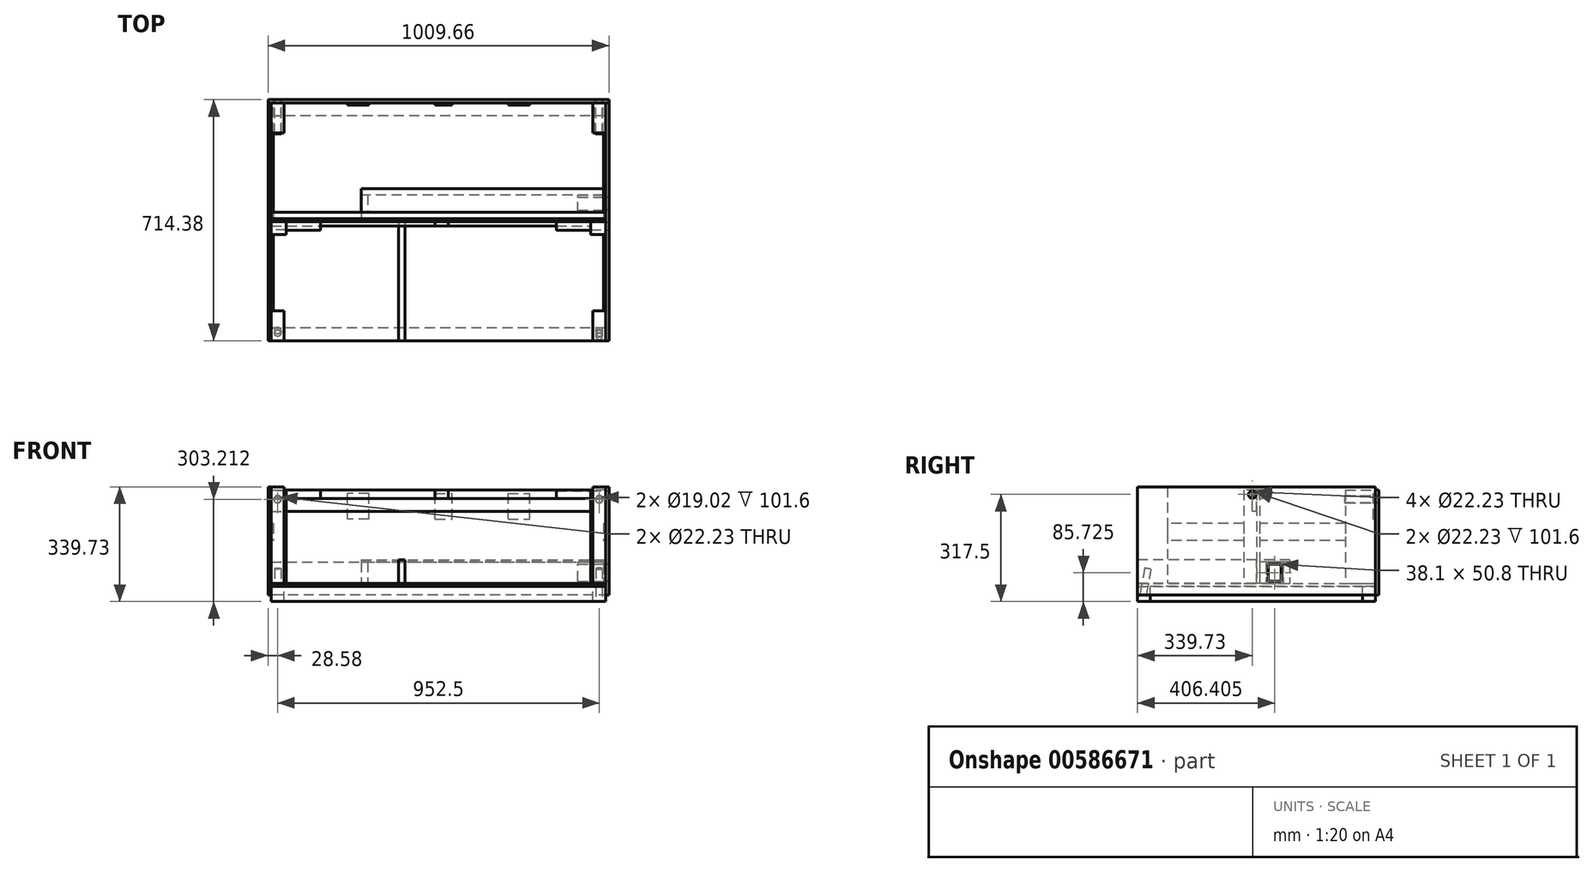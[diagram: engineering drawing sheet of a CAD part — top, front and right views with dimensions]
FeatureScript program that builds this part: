
annotation { "Feature Type Name" : "Feature", "Feature Type Description" : "" }
export const myFeature = defineFeature(function(context is Context, id is Id, definition is map)
    precondition{}
    {
        {
            var Q0;
            Q0=qCreatedBy(makeId("Right.planeOp"),FACE);
            var sketch = newSketch(context, id + "F0", { "sketchPlane" : qUnion([Q0])});
            skLineSegment(sketch, "E0.bottom", {"start": v(-352.43, 0) * mm, "end": v(-314.33, 0) * mm});
            skLineSegment(sketch, "E0.top", {"start": v(-352.43, 44.45) * mm, "end": v(-314.33, 44.45) * mm});
            skLineSegment(sketch, "E0.left", {"start": v(-352.43, 0) * mm, "end": v(-352.43, 44.45) * mm});
            skLineSegment(sketch, "E0.right", {"start": v(-314.33, 0) * mm, "end": v(-314.33, 44.45) * mm});
            skSolve(sketch);
        }
        {
            var Q0;
            Q0 = qSketchRegion(id + "F0", true);
            extrude(context, id + "F1", {"entities" : qUnion([Q0]), "endBound" : BoundingType.SYMMETRIC, "depth" : 990.6 * mm, "offsetDistance" : 25.4 * mm});
        }
        {
            var Q0;
            Q0=makeQuery(id+"F1.opExtrude","SWEPT_BODY",BODY,{"disambiguationData":[OSD([sQuery(id+"F0.wireOp",EDGE,"E0.bottom"),sQuery(id+"F0.wireOp",EDGE,"E0.top"),sQuery(id+"F0.wireOp",EDGE,"E0.left"),sQuery(id+"F0.wireOp",EDGE,"E0.right")])]});
            var Q1;
            Q1=qCreatedBy(makeId("Front.planeOp"),FACE);
            mirror(context, id + "F2", {"entities" : qUnion([Q0]), "mirrorPlane" : qUnion([Q1])});
        }
        {
            var Q0;
            Q0=makeQuery(id+"F1.opExtrude","SWEPT_FACE",FACE,{"disambiguationData":[OSD([sQuery(id+"F0.wireOp",EDGE,"E0.right")])]});
            var sketch = newSketch(context, id + "F3", { "sketchPlane" : qUnion([Q0])});
            skLineSegment(sketch, "E1.bottom", {"start": v(-495.3, 0) * mm, "end": v(-457.2, 0) * mm});
            skLineSegment(sketch, "E1.top", {"start": v(-495.3, 44.45) * mm, "end": v(-457.2, 44.45) * mm});
            skLineSegment(sketch, "E1.left", {"start": v(-495.3, 0) * mm, "end": v(-495.3, 44.45) * mm});
            skLineSegment(sketch, "E1.right", {"start": v(-457.2, 0) * mm, "end": v(-457.2, 44.45) * mm});
            skSolve(sketch);
        }
        {
            var Q0;
            Q0 = qSketchRegion(id + "F3", true);
            var Q1;
            Q1=makeQuery(id+"F2.opPattern","COPY",FACE,{"derivedFrom":makeQuery(id+"F1.opExtrude","SWEPT_FACE",FACE,{"disambiguationData":[OSD([sQuery(id+"F0.wireOp",EDGE,"E0.right")])]}),"instanceName":"1"});
            extrude(context, id + "F4", {"entities" : qUnion([Q0]), "endBound" : BoundingType.UP_TO_SURFACE, "depth" : 25.4 * mm, "endBoundEntityFace" : qUnion([Q1]), "offsetDistance" : 25.4 * mm});
        }
        {
            var Q0;
            Q0=makeQuery(id+"F4.opExtrude","SWEPT_BODY",BODY,{"disambiguationData":[OSD([sQuery(id+"F3.wireOp",EDGE,"E1.bottom"),sQuery(id+"F3.wireOp",EDGE,"E1.top"),sQuery(id+"F3.wireOp",EDGE,"E1.left"),sQuery(id+"F3.wireOp",EDGE,"E1.right")])]});
            var Q1;
            Q1=qCreatedBy(makeId("Right.planeOp"),FACE);
            mirror(context, id + "F5", {"entities" : qUnion([Q0]), "mirrorPlane" : qUnion([Q1])});
        }
        {
            var Q0;
            Q0=makeQuery(id+"F1.opExtrude","SWEPT_FACE",FACE,{"disambiguationData":[OSD([sQuery(id+"F0.wireOp",EDGE,"E0.top")])]});
            var sketch = newSketch(context, id + "F6", { "sketchPlane" : qUnion([Q0])});
            skLineSegment(sketch, "E2.bottom", {"start": v(-495.3, -352.43) * mm, "end": v(495.3, -352.43) * mm});
            skLineSegment(sketch, "E2.top", {"start": v(-495.3, 352.43) * mm, "end": v(495.3, 352.43) * mm});
            skLineSegment(sketch, "E2.left", {"start": v(-495.3, -352.43) * mm, "end": v(-495.3, 352.43) * mm});
            skLineSegment(sketch, "E2.right", {"start": v(495.3, -352.43) * mm, "end": v(495.3, 352.43) * mm});
            skSolve(sketch);
        }
        {
            var Q0;
            Q0 = qSketchRegion(id + "F6", true);
            extrude(context, id + "F7", {"entities" : qUnion([Q0]), "depth" : 9.52 * mm, "offsetDistance" : 25.4 * mm});
        }
        {
            var Q0;
            Q0=makeQuery(id+"F2.opPattern","COPY",FACE,{"derivedFrom":makeQuery(id+"F1.opExtrude","SWEPT_FACE",FACE,{"disambiguationData":[OSD([sQuery(id+"F0.wireOp",EDGE,"E0.left")])]}),"instanceName":"1"});
            var sketch = newSketch(context, id + "F8", { "sketchPlane" : qUnion([Q0])});
            skLineSegment(sketch, "E3.bottom", {"start": v(-504.83, 19.05) * mm, "end": v(504.83, 19.05) * mm});
            skLineSegment(sketch, "E3.top", {"start": v(-504.83, 330.2) * mm, "end": v(504.83, 330.2) * mm});
            skLineSegment(sketch, "E3.left", {"start": v(-504.83, 19.05) * mm, "end": v(-504.83, 330.2) * mm});
            skLineSegment(sketch, "E3.right", {"start": v(504.83, 19.05) * mm, "end": v(504.83, 330.2) * mm});
            skSolve(sketch);
        }
        {
            var Q0;
            Q0 = qSketchRegion(id + "F8", true);
            extrude(context, id + "F9", {"entities" : qUnion([Q0]), "depth" : 9.52 * mm, "offsetDistance" : 25.4 * mm});
        }
        {
            var Q0;
            Q0=makeQuery(id+"F1.opExtrude","CAP_FACE",FACE,{"disambiguationData":[OSD([sQuery(id+"F0.wireOp",EDGE,"E0.bottom"),sQuery(id+"F0.wireOp",EDGE,"E0.top"),sQuery(id+"F0.wireOp",EDGE,"E0.left"),sQuery(id+"F0.wireOp",EDGE,"E0.right")])],"isStart":false});
            var sketch = newSketch(context, id + "F10", { "sketchPlane" : qUnion([Q0])});
            skLineSegment(sketch, "E4.bottom", {"start": v(-352.43, 19.05) * mm, "end": v(352.43, 19.05) * mm});
            skLineSegment(sketch, "E4.top", {"start": v(-352.43, 339.73) * mm, "end": v(352.43, 339.73) * mm});
            skLineSegment(sketch, "E4.left", {"start": v(-352.43, 19.05) * mm, "end": v(-352.43, 339.73) * mm});
            skLineSegment(sketch, "E4.right", {"start": v(352.43, 19.05) * mm, "end": v(352.43, 339.73) * mm});
            skSolve(sketch);
        }
        {
            var Q0;
            Q0 = qSketchRegion(id + "F10", true);
            extrude(context, id + "F11", {"entities" : qUnion([Q0]), "depth" : 9.52 * mm, "offsetDistance" : 25.4 * mm});
        }
        {
            var Q0;
            Q0=makeQuery(id+"F7.opExtrude","CAP_FACE",FACE,{"disambiguationData":[OSD([sQuery(id+"F6.wireOp",EDGE,"E2.bottom"),sQuery(id+"F6.wireOp",EDGE,"E2.top"),sQuery(id+"F6.wireOp",EDGE,"E2.left"),sQuery(id+"F6.wireOp",EDGE,"E2.right")])],"isStart":false});
            var sketch = newSketch(context, id + "F12", { "sketchPlane" : qUnion([Q0])});
            skLineSegment(sketch, "E5.bottom", {"start": v(495.3, -352.43) * mm, "end": v(457.2, -352.43) * mm});
            skLineSegment(sketch, "E5.top", {"start": v(495.3, -263.53) * mm, "end": v(457.2, -263.53) * mm});
            skLineSegment(sketch, "E5.left", {"start": v(495.3, -352.43) * mm, "end": v(495.3, -263.53) * mm});
            skLineSegment(sketch, "E5.right", {"start": v(457.2, -352.43) * mm, "end": v(457.2, -263.53) * mm});
            skSolve(sketch);
        }
        {
            var Q0;
            Q0 = qSketchRegion(id + "F12", true);
            var Q1;
            Q1=makeQuery(id+"F11.opExtrude","SWEPT_FACE",FACE,{"disambiguationData":[OSD([sQuery(id+"F10.wireOp",EDGE,"E4.top")])]});
            extrude(context, id + "F13", {"entities" : qUnion([Q0]), "endBound" : BoundingType.UP_TO_SURFACE, "depth" : 25.4 * mm, "endBoundEntityFace" : qUnion([Q1]), "offsetDistance" : 25.4 * mm});
        }
        {
            var Q0;
            Q0=makeQuery(id+"F7.opExtrude","CAP_FACE",FACE,{"disambiguationData":[OSD([sQuery(id+"F6.wireOp",EDGE,"E2.bottom"),sQuery(id+"F6.wireOp",EDGE,"E2.top"),sQuery(id+"F6.wireOp",EDGE,"E2.left"),sQuery(id+"F6.wireOp",EDGE,"E2.right")])],"isStart":false});
            var sketch = newSketch(context, id + "F14", { "sketchPlane" : qUnion([Q0])});
            skLineSegment(sketch, "E6.bottom", {"start": v(495.3, 352.43) * mm, "end": v(457.2, 352.43) * mm});
            skLineSegment(sketch, "E6.top", {"start": v(495.3, 263.53) * mm, "end": v(457.2, 263.53) * mm});
            skLineSegment(sketch, "E6.left", {"start": v(495.3, 352.43) * mm, "end": v(495.3, 263.53) * mm});
            skLineSegment(sketch, "E6.right", {"start": v(457.2, 352.43) * mm, "end": v(457.2, 263.53) * mm});
            skSolve(sketch);
        }
        {
            var Q0;
            Q0 = qSketchRegion(id + "F14", true);
            var Q1;
            Q1=makeQuery(id+"F9.opExtrude","SWEPT_FACE",FACE,{"disambiguationData":[OSD([sQuery(id+"F8.wireOp",EDGE,"E3.top")])]});
            extrude(context, id + "F15", {"entities" : qUnion([Q0]), "endBound" : BoundingType.UP_TO_SURFACE, "depth" : 25.4 * mm, "endBoundEntityFace" : qUnion([Q1]), "offsetDistance" : 25.4 * mm});
        }
        {
            var Q0;
            Q0=makeQuery(id+"F7.opExtrude","CAP_FACE",FACE,{"disambiguationData":[OSD([sQuery(id+"F6.wireOp",EDGE,"E2.bottom"),sQuery(id+"F6.wireOp",EDGE,"E2.top"),sQuery(id+"F6.wireOp",EDGE,"E2.left"),sQuery(id+"F6.wireOp",EDGE,"E2.right")])],"isStart":false});
            var sketch = newSketch(context, id + "F16", { "sketchPlane" : qUnion([Q0])});
            skLineSegment(sketch, "E7.bottom", {"start": v(495.3, 0) * mm, "end": v(450.85, 0) * mm});
            skLineSegment(sketch, "E7.top", {"start": v(495.3, -38.1) * mm, "end": v(450.85, -38.1) * mm});
            skLineSegment(sketch, "E7.left", {"start": v(495.3, 0) * mm, "end": v(495.3, -38.1) * mm});
            skLineSegment(sketch, "E7.right", {"start": v(450.85, 0) * mm, "end": v(450.85, -38.1) * mm});
            skSolve(sketch);
        }
        {
            var Q0;
            Q0 = qSketchRegion(id + "F16", true);
            var Q1;
            Q1=makeQuery(id+"F9.opExtrude","SWEPT_FACE",FACE,{"disambiguationData":[OSD([sQuery(id+"F8.wireOp",EDGE,"E3.top")])]});
            extrude(context, id + "F17", {"entities" : qUnion([Q0]), "endBound" : BoundingType.UP_TO_SURFACE, "depth" : 25.4 * mm, "endBoundEntityFace" : qUnion([Q1]), "offsetDistance" : 25.4 * mm});
        }
        {
            var Q0;
            Q0=makeQuery(id+"F17.opExtrude","SWEPT_FACE",FACE,{"disambiguationData":[OSD([sQuery(id+"F16.wireOp",EDGE,"E7.bottom")])]});
            var sketch = newSketch(context, id + "F18", { "sketchPlane" : qUnion([Q0])});
            skLineSegment(sketch, "E8.bottom", {"start": v(-495.3, 53.98) * mm, "end": v(495.3, 53.98) * mm});
            skLineSegment(sketch, "E8.top", {"start": v(-495.3, 330.2) * mm, "end": v(495.3, 330.2) * mm});
            skLineSegment(sketch, "E8.left", {"start": v(-495.3, 53.98) * mm, "end": v(-495.3, 330.2) * mm});
            skLineSegment(sketch, "E8.right", {"start": v(495.3, 53.98) * mm, "end": v(495.3, 330.2) * mm});
            skSolve(sketch);
        }
        {
            var Q0;
            Q0 = qSketchRegion(id + "F18", true);
            extrude(context, id + "F19", {"entities" : qUnion([Q0]), "depth" : 9.52 * mm, "offsetDistance" : 25.4 * mm});
        }
        {
            var Q0;
            Q0=makeQuery(id+"F17.opExtrude","SWEPT_FACE",FACE,{"disambiguationData":[OSD([sQuery(id+"F16.wireOp",EDGE,"E7.right")])]});
            var sketch = newSketch(context, id + "F20", { "sketchPlane" : qUnion([Q0])});
            skLineSegment(sketch, "E9.bottom", {"start": v(12.7, 304.8) * mm, "end": v(0, 304.8) * mm});
            skLineSegment(sketch, "E9.top", {"start": v(12.7, 266.7) * mm, "end": v(0, 266.7) * mm});
            skLineSegment(sketch, "E9.left", {"start": v(12.7, 304.8) * mm, "end": v(12.7, 266.7) * mm});
            skLineSegment(sketch, "E9.right", {"start": v(0, 304.8) * mm, "end": v(0, 266.7) * mm});
            skSolve(sketch);
        }
        {
            var Q0;
            Q0 = qSketchRegion(id + "F20", true);
            var Q1;
            Q1=makeQuery(id+"F19.opExtrude","SWEPT_FACE",FACE,{"disambiguationData":[OSD([sQuery(id+"F18.wireOp",EDGE,"E8.right")])]});
            extrude(context, id + "F21", {"entities" : qUnion([Q0]), "endBound" : BoundingType.UP_TO_SURFACE, "depth" : 25.4 * mm, "endBoundEntityFace" : qUnion([Q1]), "offsetDistance" : 25.4 * mm});
        }
        {
            var Q0;
            Q0=makeQuery(id+"F1.opExtrude","SWEPT_FACE",FACE,{"disambiguationData":[OSD([sQuery(id+"F0.wireOp",EDGE,"E0.left")])]});
            var sketch = newSketch(context, id + "F22", { "sketchPlane" : qUnion([Q0])});
            skLineSegment(sketch, "E10.bottom", {"start": v(-118.36, 53.98) * mm, "end": v(-99.31, 53.98) * mm});
            skLineSegment(sketch, "E10.top", {"start": v(-118.36, 123.83) * mm, "end": v(-99.31, 123.83) * mm});
            skLineSegment(sketch, "E10.left", {"start": v(-118.36, 53.98) * mm, "end": v(-118.36, 123.83) * mm});
            skLineSegment(sketch, "E10.right", {"start": v(-99.31, 53.98) * mm, "end": v(-99.31, 123.83) * mm});
            skSolve(sketch);
        }
        {
            var Q0;
            Q0 = qSketchRegion(id + "F22", true);
            var Q1;
            Q1=makeQuery(id+"F19.opExtrude","CAP_FACE",FACE,{"disambiguationData":[OSD([sQuery(id+"F18.wireOp",EDGE,"E8.bottom"),sQuery(id+"F18.wireOp",EDGE,"E8.top"),sQuery(id+"F18.wireOp",EDGE,"E8.left"),sQuery(id+"F18.wireOp",EDGE,"E8.right")])],"isStart":true});
            extrude(context, id + "F23", {"entities" : qUnion([Q0]), "endBound" : BoundingType.UP_TO_SURFACE, "oppositeDirection" : true, "depth" : 25.4 * mm, "endBoundEntityFace" : qUnion([Q1]), "offsetDistance" : 25.4 * mm});
        }
        {
            var Q0;
            Q0=makeQuery(id+"F11.opExtrude","CAP_FACE",FACE,{"disambiguationData":[OSD([sQuery(id+"F10.wireOp",EDGE,"E4.bottom"),sQuery(id+"F10.wireOp",EDGE,"E4.top"),sQuery(id+"F10.wireOp",EDGE,"E4.left"),sQuery(id+"F10.wireOp",EDGE,"E4.right")])],"isStart":true});
            var sketch = newSketch(context, id + "F24", { "sketchPlane" : qUnion([Q0])});
            skLineSegment(sketch, "E11.bottom", {"start": v(-9.52, 53.98) * mm, "end": v(-28.57, 53.98) * mm});
            skLineSegment(sketch, "E11.top", {"start": v(-9.53, 117.48) * mm, "end": v(-28.58, 117.48) * mm});
            skLineSegment(sketch, "E11.left", {"start": v(-9.52, 53.98) * mm, "end": v(-9.53, 117.48) * mm});
            skLineSegment(sketch, "E11.right", {"start": v(-28.57, 53.98) * mm, "end": v(-28.58, 117.48) * mm});
            skSolve(sketch);
        }
        {
            var Q0;
            Q0 = qSketchRegion(id + "F24", true);
            var Q1;
            Q1=makeQuery(id+"F1.opExtrude","CAP_FACE",FACE,{"disambiguationData":[OSD([sQuery(id+"F0.wireOp",EDGE,"E0.bottom"),sQuery(id+"F0.wireOp",EDGE,"E0.top"),sQuery(id+"F0.wireOp",EDGE,"E0.left"),sQuery(id+"F0.wireOp",EDGE,"E0.right")])],"isStart":true});
            extrude(context, id + "F25", {"entities" : qUnion([Q0]), "endBound" : BoundingType.UP_TO_SURFACE, "depth" : 25.4 * mm, "endBoundEntityFace" : qUnion([Q1]), "offsetDistance" : 25.4 * mm});
        }
        {
            var Q0;
            Q0=makeQuery(id+"F11.opExtrude","CAP_FACE",FACE,{"disambiguationData":[OSD([sQuery(id+"F10.wireOp",EDGE,"E4.bottom"),sQuery(id+"F10.wireOp",EDGE,"E4.top"),sQuery(id+"F10.wireOp",EDGE,"E4.left"),sQuery(id+"F10.wireOp",EDGE,"E4.right")])],"isStart":true});
            var sketch = newSketch(context, id + "F26", { "sketchPlane" : qUnion([Q0])});
            skLineSegment(sketch, "E12.bottom", {"start": v(-9.53, 330.2) * mm, "end": v(-28.58, 330.2) * mm});
            skLineSegment(sketch, "E12.top", {"start": v(-9.52, 304.8) * mm, "end": v(-28.57, 304.8) * mm});
            skLineSegment(sketch, "E12.left", {"start": v(-9.53, 330.2) * mm, "end": v(-9.52, 304.8) * mm});
            skLineSegment(sketch, "E12.right", {"start": v(-28.58, 330.2) * mm, "end": v(-28.57, 304.8) * mm});
            skSolve(sketch);
        }
        {
            var Q0;
            Q0 = qSketchRegion(id + "F26", true);
            var Q1;
            Q1=makeQuery(id+"F1.opExtrude","CAP_FACE",FACE,{"disambiguationData":[OSD([sQuery(id+"F0.wireOp",EDGE,"E0.bottom"),sQuery(id+"F0.wireOp",EDGE,"E0.top"),sQuery(id+"F0.wireOp",EDGE,"E0.left"),sQuery(id+"F0.wireOp",EDGE,"E0.right")])],"isStart":true});
            extrude(context, id + "F27", {"entities" : qUnion([Q0]), "endBound" : BoundingType.UP_TO_SURFACE, "depth" : 25.4 * mm, "endBoundEntityFace" : qUnion([Q1]), "offsetDistance" : 25.4 * mm});
        }
        {
            var Q0;
            Q0=makeQuery(id+"F17.opExtrude","SWEPT_FACE",FACE,{"disambiguationData":[OSD([sQuery(id+"F16.wireOp",EDGE,"E7.right")])]});
            var sketch = newSketch(context, id + "F28", { "sketchPlane" : qUnion([Q0])});
            skCircle(sketch, "E13", {"center": v(12.7, 317.5) * mm, "radius": 12.7 * mm});
            skCircle(sketch, "E14", {"center": v(12.7, 317.5) * mm, "radius": 11.11 * mm});
            skSolve(sketch);
        }
        {
            var Q0;
            Q0=makeQuery(id+"F11.opExtrude","CAP_FACE",FACE,{"disambiguationData":[OSD([sQuery(id+"F10.wireOp",EDGE,"E4.bottom"),sQuery(id+"F10.wireOp",EDGE,"E4.top"),sQuery(id+"F10.wireOp",EDGE,"E4.left"),sQuery(id+"F10.wireOp",EDGE,"E4.right")])],"isStart":false});
            var sketch = newSketch(context, id + "F29", { "sketchPlane" : qUnion([Q0])});
            skCircle(sketch, "E15", {"center": v(-12.7, 317.5) * mm, "radius": 11.11 * mm});
            skSolve(sketch);
        }
        {
            var Q0;
            Q0 = qSketchRegion(id + "F29", true);
            var Q1;
            Q1=makeQuery(id+"F17.opExtrude","SWEPT_FACE",FACE,{"disambiguationData":[OSD([sQuery(id+"F16.wireOp",EDGE,"E7.right")])]});
            extrude(context, id + "F30", {"entities" : qUnion([Q0]), "operationType" : NewBodyOperationType.REMOVE, "endBound" : BoundingType.UP_TO_SURFACE, "oppositeDirection" : true, "depth" : 25.4 * mm, "endBoundEntityFace" : qUnion([Q1]), "offsetDistance" : 25.4 * mm});
        }
        {
            var Q0;
            Q0 = qSketchRegion(id + "F28", true);
            extrude(context, id + "F31", {"entities" : qUnion([Q0]), "depth" : 101.6 * mm, "offsetDistance" : 25.4 * mm});
        }
        {
            var Q0;
            Q0=makeQuery(id+"F13.opExtrude","SWEPT_FACE",FACE,{"disambiguationData":[OSD([sQuery(id+"F12.wireOp",EDGE,"E5.top")])]});
            var sketch = newSketch(context, id + "F32", { "sketchPlane" : qUnion([Q0])});
            skLineSegment(sketch, "E16.bottom", {"start": v(-488.95, 180.98) * mm, "end": v(-495.3, 180.98) * mm});
            skLineSegment(sketch, "E16.top", {"start": v(-488.95, 231.78) * mm, "end": v(-495.3, 231.78) * mm});
            skLineSegment(sketch, "E16.left", {"start": v(-488.95, 180.98) * mm, "end": v(-488.95, 231.78) * mm});
            skLineSegment(sketch, "E16.right", {"start": v(-495.3, 180.98) * mm, "end": v(-495.3, 231.78) * mm});
            skSolve(sketch);
        }
        {
            var Q0;
            Q0 = qSketchRegion(id + "F32", true);
            var Q1;
            Q1=makeQuery(id+"F17.opExtrude","SWEPT_FACE",FACE,{"disambiguationData":[OSD([sQuery(id+"F16.wireOp",EDGE,"E7.top")])]});
            extrude(context, id + "F33", {"entities" : qUnion([Q0]), "endBound" : BoundingType.UP_TO_SURFACE, "depth" : 25.4 * mm, "endBoundEntityFace" : qUnion([Q1]), "offsetDistance" : 25.4 * mm});
        }
        {
            var Q0;
            Q0=makeQuery(id+"F19.opExtrude","CAP_FACE",FACE,{"disambiguationData":[OSD([sQuery(id+"F18.wireOp",EDGE,"E8.bottom"),sQuery(id+"F18.wireOp",EDGE,"E8.top"),sQuery(id+"F18.wireOp",EDGE,"E8.left"),sQuery(id+"F18.wireOp",EDGE,"E8.right")])],"isStart":false});
            var sketch = newSketch(context, id + "F34", { "sketchPlane" : qUnion([Q0])});
            skLineSegment(sketch, "E17.bottom", {"start": v(-495.3, 180.98) * mm, "end": v(-488.95, 180.98) * mm});
            skLineSegment(sketch, "E17.top", {"start": v(-495.3, 231.78) * mm, "end": v(-488.95, 231.78) * mm});
            skLineSegment(sketch, "E17.left", {"start": v(-495.3, 180.98) * mm, "end": v(-495.3, 231.78) * mm});
            skLineSegment(sketch, "E17.right", {"start": v(-488.95, 180.98) * mm, "end": v(-488.95, 231.78) * mm});
            skSolve(sketch);
        }
        {
            var Q0;
            Q0 = qSketchRegion(id + "F34", true);
            var Q1;
            Q1=makeQuery(id+"F15.opExtrude","SWEPT_FACE",FACE,{"disambiguationData":[OSD([sQuery(id+"F14.wireOp",EDGE,"E6.top")])]});
            extrude(context, id + "F35", {"entities" : qUnion([Q0]), "endBound" : BoundingType.UP_TO_SURFACE, "depth" : 25.4 * mm, "endBoundEntityFace" : qUnion([Q1]), "offsetDistance" : 25.4 * mm});
        }
        {
            var Q0;
            Q0=makeQuery(id+"F9.opExtrude","CAP_FACE",FACE,{"disambiguationData":[OSD([sQuery(id+"F8.wireOp",EDGE,"E3.bottom"),sQuery(id+"F8.wireOp",EDGE,"E3.top"),sQuery(id+"F8.wireOp",EDGE,"E3.left"),sQuery(id+"F8.wireOp",EDGE,"E3.right")])],"isStart":true});
            var sketch = newSketch(context, id + "F36", { "sketchPlane" : qUnion([Q0])});
            skLineSegment(sketch, "E18.bottom", {"start": v(206.38, 244.48) * mm, "end": v(269.88, 244.48) * mm});
            skLineSegment(sketch, "E18.top", {"start": v(206.38, 320.68) * mm, "end": v(269.88, 320.68) * mm});
            skLineSegment(sketch, "E18.left", {"start": v(206.37, 244.48) * mm, "end": v(206.37, 320.68) * mm});
            skLineSegment(sketch, "E18.right", {"start": v(269.87, 244.48) * mm, "end": v(269.87, 320.68) * mm});
            skSolve(sketch);
        }
        {
            var Q0;
            Q0 = qSketchRegion(id + "F36", true);
            extrude(context, id + "F37", {"entities" : qUnion([Q0]), "operationType" : NewBodyOperationType.ADD, "depth" : 6.35 * mm, "offsetDistance" : 25.4 * mm});
        }
        {
            var Q0;
            Q0=makeQuery(id+"F9.opExtrude","CAP_FACE",FACE,{"disambiguationData":[OSD([sQuery(id+"F8.wireOp",EDGE,"E3.bottom"),sQuery(id+"F8.wireOp",EDGE,"E3.top"),sQuery(id+"F8.wireOp",EDGE,"E3.left"),sQuery(id+"F8.wireOp",EDGE,"E3.right")])],"isStart":false});
            var sketch = newSketch(context, id + "F38", { "sketchPlane" : qUnion([Q0])});
            skCircle(sketch, "E19", {"center": v(-476.25, 303.21) * mm, "radius": 11.11 * mm});
            skSolve(sketch);
        }
        {
            var Q0;
            Q0 = qSketchRegion(id + "F38", true);
            var Q1;
            Q1=makeQuery(id+"F15.opExtrude","SWEPT_FACE",FACE,{"disambiguationData":[OSD([sQuery(id+"F14.wireOp",EDGE,"E6.top")])]});
            extrude(context, id + "F39", {"entities" : qUnion([Q0]), "operationType" : NewBodyOperationType.REMOVE, "endBound" : BoundingType.UP_TO_SURFACE, "oppositeDirection" : true, "depth" : 25.4 * mm, "endBoundEntityFace" : qUnion([Q1]), "offsetDistance" : 25.4 * mm});
        }
        {
            var Q0;
            Q0=makeQuery(id+"F9.opExtrude","CAP_FACE",FACE,{"disambiguationData":[OSD([sQuery(id+"F8.wireOp",EDGE,"E3.bottom"),sQuery(id+"F8.wireOp",EDGE,"E3.top"),sQuery(id+"F8.wireOp",EDGE,"E3.left"),sQuery(id+"F8.wireOp",EDGE,"E3.right")])],"isStart":false});
            var sketch = newSketch(context, id + "F40", { "sketchPlane" : qUnion([Q0])});
            skCircle(sketch, "E20", {"center": v(-476.25, 303.21) * mm, "radius": 11.11 * mm});
            skCircle(sketch, "E21.0", {"center": v(-476.25, 303.21) * mm, "radius": 9.51 * mm});
            skSolve(sketch);
        }
        {
            var Q0;
            Q0 = qSketchRegion(id + "F40", true);
            extrude(context, id + "F41", {"entities" : qUnion([Q0]), "oppositeDirection" : true, "depth" : 101.6 * mm, "offsetDistance" : 25.4 * mm});
        }
        {
            var Q0;
            Q0=makeQuery(id+"F1.opExtrude","SWEPT_EDGE",EDGE,{"disambiguationData":[OSD([sQuery(id+"F0.wireOp",EDGE,"E0.bottom"),sQuery(id+"F0.wireOp",EDGE,"E0.left")])]});
            cPlane(context, id + "F42", {"entities" : qUnion([Q0]), "cplaneType" : CPlaneType.LINE_ANGLE, "offset" : 25.4 * mm, "angle" : 80 * degree, "oppositeDirection" : true, "width" : 152.4 * mm, "height" : 152.4 * mm});
        }
        {
            var Q0;
            Q0=qCreatedBy(id+"F42.planeOp",FACE);
            var sketch = newSketch(context, id + "F43", { "sketchPlane" : qUnion([Q0])});
            skCircle(sketch, "E22", {"center": v(476.25, 334.37) * mm, "radius": 9.53 * mm});
            skSolve(sketch);
        }
        {
            var Q0;
            Q0 = qSketchRegion(id + "F43", true);
            extrude(context, id + "F44", {"entities" : qUnion([Q0]), "operationType" : NewBodyOperationType.REMOVE, "oppositeDirection" : true, "depth" : 101.6 * mm, "offsetDistance" : 25.4 * mm});
        }
        {
            var Q0;
            Q0=makeQuery(id+"F11.opExtrude","SWEPT_BODY",BODY,{"disambiguationData":[OSD([sQuery(id+"F10.wireOp",EDGE,"E4.bottom"),sQuery(id+"F10.wireOp",EDGE,"E4.top"),sQuery(id+"F10.wireOp",EDGE,"E4.left"),sQuery(id+"F10.wireOp",EDGE,"E4.right")])]});
            var Q1;
            Q1=makeQuery(id+"F13.opExtrude","SWEPT_BODY",BODY,{"disambiguationData":[OSD([sQuery(id+"F12.wireOp",EDGE,"E5.bottom"),sQuery(id+"F12.wireOp",EDGE,"E5.top"),sQuery(id+"F12.wireOp",EDGE,"E5.left"),sQuery(id+"F12.wireOp",EDGE,"E5.right")])]});
            var Q2;
            Q2=makeQuery(id+"F17.opExtrude","SWEPT_BODY",BODY,{"disambiguationData":[OSD([sQuery(id+"F16.wireOp",EDGE,"E7.bottom"),sQuery(id+"F16.wireOp",EDGE,"E7.top"),sQuery(id+"F16.wireOp",EDGE,"E7.left"),sQuery(id+"F16.wireOp",EDGE,"E7.right")])]});
            var Q3;
            Q3=makeQuery(id+"F15.opExtrude","SWEPT_BODY",BODY,{"disambiguationData":[OSD([sQuery(id+"F14.wireOp",EDGE,"E6.bottom"),sQuery(id+"F14.wireOp",EDGE,"E6.top"),sQuery(id+"F14.wireOp",EDGE,"E6.left"),sQuery(id+"F14.wireOp",EDGE,"E6.right")])]});
            var Q4;
            Q4=makeQuery(id+"F31.opExtrude","SWEPT_BODY",BODY,{"disambiguationData":[OSD([sQuery(id+"F28.wireOp",EDGE,"E13"),sQuery(id+"F28.wireOp",EDGE,"E14")])]});
            var Q5;
            Q5=makeQuery(id+"F33.opExtrude","SWEPT_BODY",BODY,{"disambiguationData":[OSD([sQuery(id+"F32.wireOp",EDGE,"E16.bottom"),sQuery(id+"F32.wireOp",EDGE,"E16.top"),sQuery(id+"F32.wireOp",EDGE,"E16.left"),sQuery(id+"F32.wireOp",EDGE,"E16.right")])]});
            var Q6;
            Q6=makeQuery(id+"F35.opExtrude","SWEPT_BODY",BODY,{"disambiguationData":[OSD([sQuery(id+"F34.wireOp",EDGE,"E17.bottom"),sQuery(id+"F34.wireOp",EDGE,"E17.top"),sQuery(id+"F34.wireOp",EDGE,"E17.left"),sQuery(id+"F34.wireOp",EDGE,"E17.right")])]});
            var Q7;
            Q7=makeQuery(id+"F9.opExtrude","SWEPT_BODY",BODY,{"disambiguationData":[OSD([sQuery(id+"F8.wireOp",EDGE,"E3.bottom"),sQuery(id+"F8.wireOp",EDGE,"E3.top"),sQuery(id+"F8.wireOp",EDGE,"E3.left"),sQuery(id+"F8.wireOp",EDGE,"E3.right")])]});
            var Q8;
            Q8=makeQuery(id+"F41.opExtrude","SWEPT_BODY",BODY,{"disambiguationData":[OSD([sQuery(id+"F40.wireOp",EDGE,"E20"),sQuery(id+"F40.wireOp",EDGE,"E21.0")])]});
            var Q9;
            Q9=qCreatedBy(makeId("Right.planeOp"),FACE);
            mirror(context, id + "F45", {"entities" : qUnion([Q0, Q1, Q2, Q3, Q4, Q5, Q6, Q7, Q8]), "mirrorPlane" : qUnion([Q9])});
        }
        {
            var Q0;
            Q0=makeQuery(id+"F9.opExtrude","CAP_FACE",FACE,{"disambiguationData":[OSD([sQuery(id+"F8.wireOp",EDGE,"E3.bottom"),sQuery(id+"F8.wireOp",EDGE,"E3.top"),sQuery(id+"F8.wireOp",EDGE,"E3.left"),sQuery(id+"F8.wireOp",EDGE,"E3.right")])],"isStart":true});
            var sketch = newSketch(context, id + "F46", { "sketchPlane" : qUnion([Q0])});
            skLineSegment(sketch, "E23.bottom", {"start": v(-9.53, 244.48) * mm, "end": v(41.28, 244.48) * mm});
            skLineSegment(sketch, "E23.top", {"start": v(-9.53, 320.68) * mm, "end": v(41.27, 320.68) * mm});
            skLineSegment(sketch, "E23.left", {"start": v(-9.53, 244.48) * mm, "end": v(-9.53, 320.68) * mm});
            skLineSegment(sketch, "E23.right", {"start": v(41.28, 244.48) * mm, "end": v(41.28, 320.68) * mm});
            skSolve(sketch);
        }
        {
            var Q0;
            Q0 = qSketchRegion(id + "F46", true);
            extrude(context, id + "F47", {"entities" : qUnion([Q0]), "operationType" : NewBodyOperationType.ADD, "depth" : 6.35 * mm, "offsetDistance" : 25.4 * mm});
        }
        {
            var Q0;
            Q0=makeQuery(id+"F19.opExtrude","CAP_FACE",FACE,{"disambiguationData":[OSD([sQuery(id+"F18.wireOp",EDGE,"E8.bottom"),sQuery(id+"F18.wireOp",EDGE,"E8.top"),sQuery(id+"F18.wireOp",EDGE,"E8.left"),sQuery(id+"F18.wireOp",EDGE,"E8.right")])],"isStart":true});
            var sketch = newSketch(context, id + "F48", { "sketchPlane" : qUnion([Q0])});
            skLineSegment(sketch, "E24.bottom", {"start": v(-9.53, 304.8) * mm, "end": v(28.57, 304.8) * mm});
            skLineSegment(sketch, "E24.top", {"start": v(-9.53, 330.2) * mm, "end": v(28.57, 330.2) * mm});
            skLineSegment(sketch, "E24.left", {"start": v(-9.53, 304.8) * mm, "end": v(-9.53, 330.2) * mm});
            skLineSegment(sketch, "E24.right", {"start": v(28.57, 304.8) * mm, "end": v(28.57, 330.2) * mm});
            skSolve(sketch);
        }
        {
            var Q0;
            Q0 = qSketchRegion(id + "F48", true);
            var Q1;
            Q1=makeQuery(id+"F21.opExtrude","SWEPT_FACE",FACE,{"disambiguationData":[OSD([sQuery(id+"F20.wireOp",EDGE,"E9.left")])]});
            extrude(context, id + "F49", {"entities" : qUnion([Q0]), "endBound" : BoundingType.UP_TO_SURFACE, "depth" : 25.4 * mm, "endBoundEntityFace" : qUnion([Q1]), "offsetDistance" : 25.4 * mm});
        }
        {
            var Q0;
            Q0=makeQuery(id+"F7.opExtrude","CAP_FACE",FACE,{"disambiguationData":[OSD([sQuery(id+"F6.wireOp",EDGE,"E2.bottom"),sQuery(id+"F6.wireOp",EDGE,"E2.top"),sQuery(id+"F6.wireOp",EDGE,"E2.left"),sQuery(id+"F6.wireOp",EDGE,"E2.right")])],"isStart":false});
            var sketch = newSketch(context, id + "F50", { "sketchPlane" : qUnion([Q0])});
            skLineSegment(sketch, "E25.bottom", {"start": v(-228.6, 28.58) * mm, "end": v(-209.55, 28.58) * mm});
            skLineSegment(sketch, "E25.top", {"start": v(-228.6, 79.38) * mm, "end": v(-209.55, 79.38) * mm});
            skLineSegment(sketch, "E25.left", {"start": v(-228.6, 28.58) * mm, "end": v(-228.6, 79.38) * mm});
            skLineSegment(sketch, "E25.right", {"start": v(-209.55, 28.58) * mm, "end": v(-209.55, 79.38) * mm});
            skSolve(sketch);
        }
        {
            var Q0;
            Q0 = qSketchRegion(id + "F50", true);
            var Q1;
            Q1=makeQuery(id+"F25.opExtrude","SWEPT_FACE",FACE,{"disambiguationData":[OSD([sQuery(id+"F24.wireOp",EDGE,"E11.top")])]});
            extrude(context, id + "F51", {"entities" : qUnion([Q0]), "endBound" : BoundingType.UP_TO_SURFACE, "depth" : 25.4 * mm, "endBoundEntityFace" : qUnion([Q1]), "offsetDistance" : 25.4 * mm});
        }
        {
            var Q0;
            Q0=makeQuery(id+"F7.opExtrude","CAP_FACE",FACE,{"disambiguationData":[OSD([sQuery(id+"F6.wireOp",EDGE,"E2.bottom"),sQuery(id+"F6.wireOp",EDGE,"E2.top"),sQuery(id+"F6.wireOp",EDGE,"E2.left"),sQuery(id+"F6.wireOp",EDGE,"E2.right")])],"isStart":false});
            var sketch = newSketch(context, id + "F52", { "sketchPlane" : qUnion([Q0])});
            skLineSegment(sketch, "E26.bottom", {"start": v(-228.6, 79.38) * mm, "end": v(488.95, 79.38) * mm});
            skLineSegment(sketch, "E26.top", {"start": v(-228.6, 98.43) * mm, "end": v(488.95, 98.43) * mm});
            skLineSegment(sketch, "E26.left", {"start": v(-228.6, 79.38) * mm, "end": v(-228.6, 98.43) * mm});
            skLineSegment(sketch, "E26.right", {"start": v(488.95, 79.38) * mm, "end": v(488.95, 98.43) * mm});
            skSolve(sketch);
        }
        {
            var Q0;
            Q0 = qSketchRegion(id + "F52", true);
            var Q1;
            Q1=makeQuery(id+"F25.opExtrude","SWEPT_FACE",FACE,{"disambiguationData":[OSD([sQuery(id+"F24.wireOp",EDGE,"E11.top")])]});
            extrude(context, id + "F53", {"entities" : qUnion([Q0]), "endBound" : BoundingType.UP_TO_SURFACE, "depth" : 25.4 * mm, "endBoundEntityFace" : qUnion([Q1]), "offsetDistance" : 25.4 * mm});
        }
        {
            var Q0;
            Q0=makeQuery(id+"F11.opExtrude","CAP_FACE",FACE,{"disambiguationData":[OSD([sQuery(id+"F10.wireOp",EDGE,"E4.bottom"),sQuery(id+"F10.wireOp",EDGE,"E4.top"),sQuery(id+"F10.wireOp",EDGE,"E4.left"),sQuery(id+"F10.wireOp",EDGE,"E4.right")])],"isStart":true});
            var sketch = newSketch(context, id + "F54", { "sketchPlane" : qUnion([Q0])});
            skLineSegment(sketch, "E27.bottom", {"start": v(-73.03, 60.33) * mm, "end": v(-34.92, 60.33) * mm});
            skLineSegment(sketch, "E27.top", {"start": v(-73.03, 111.13) * mm, "end": v(-34.93, 111.13) * mm});
            skLineSegment(sketch, "E27.left", {"start": v(-73.03, 60.33) * mm, "end": v(-73.03, 111.13) * mm});
            skLineSegment(sketch, "E27.right", {"start": v(-34.92, 60.33) * mm, "end": v(-34.93, 111.13) * mm});
            skSolve(sketch);
        }
        {
            var Q0;
            Q0 = qSketchRegion(id + "F54", true);
            extrude(context, id + "F55", {"entities" : qUnion([Q0]), "operationType" : NewBodyOperationType.REMOVE, "oppositeDirection" : true, "depth" : 25.4 * mm, "offsetDistance" : 25.4 * mm});
        }
        {
            var Q0;
            Q0=makeQuery(id+"F7.opExtrude","CAP_FACE",FACE,{"disambiguationData":[OSD([sQuery(id+"F6.wireOp",EDGE,"E2.bottom"),sQuery(id+"F6.wireOp",EDGE,"E2.top"),sQuery(id+"F6.wireOp",EDGE,"E2.left"),sQuery(id+"F6.wireOp",EDGE,"E2.right")])],"isStart":false});
            var sketch = newSketch(context, id + "F56", { "sketchPlane" : qUnion([Q0])});
            skLineSegment(sketch, "E28.bottom", {"start": v(412.75, 28.58) * mm, "end": v(488.95, 28.58) * mm});
            skLineSegment(sketch, "E28.top", {"start": v(412.75, 79.38) * mm, "end": v(488.95, 79.38) * mm});
            skLineSegment(sketch, "E28.left", {"start": v(412.75, 28.58) * mm, "end": v(412.75, 79.38) * mm});
            skLineSegment(sketch, "E28.right", {"start": v(488.95, 28.58) * mm, "end": v(488.95, 79.38) * mm});
            skSolve(sketch);
        }
        {
            var Q0;
            Q0 = qSketchRegion(id + "F56", true);
            extrude(context, id + "F57", {"entities" : qUnion([Q0]), "depth" : 6.35 * mm, "offsetDistance" : 25.4 * mm});
        }
        {
            var Q0;
            Q0=makeQuery(id+"F25.opExtrude","SWEPT_FACE",FACE,{"disambiguationData":[OSD([sQuery(id+"F24.wireOp",EDGE,"E11.right")])]});
            var sketch = newSketch(context, id + "F58", { "sketchPlane" : qUnion([Q0])});
            skLineSegment(sketch, "E29.bottom", {"start": v(-412.75, 111.13) * mm, "end": v(-488.95, 111.13) * mm});
            skLineSegment(sketch, "E29.top", {"start": v(-412.75, 60.33) * mm, "end": v(-488.95, 60.33) * mm});
            skLineSegment(sketch, "E29.left", {"start": v(-412.75, 111.13) * mm, "end": v(-412.75, 60.33) * mm});
            skLineSegment(sketch, "E29.right", {"start": v(-488.95, 111.13) * mm, "end": v(-488.95, 60.33) * mm});
            skSolve(sketch);
        }
        {
            var Q0;
            Q0 = qSketchRegion(id + "F58", true);
            extrude(context, id + "F59", {"entities" : qUnion([Q0]), "depth" : 6.35 * mm, "offsetDistance" : 25.4 * mm});
        }
        {
            var Q0;
            Q0=makeQuery(id+"F53.opExtrude","SWEPT_FACE",FACE,{"disambiguationData":[OSD([sQuery(id+"F52.wireOp",EDGE,"E26.bottom")])]});
            var sketch = newSketch(context, id + "F60", { "sketchPlane" : qUnion([Q0])});
            skLineSegment(sketch, "E30.bottom", {"start": v(412.75, 60.33) * mm, "end": v(488.95, 60.33) * mm});
            skLineSegment(sketch, "E30.top", {"start": v(412.75, 111.13) * mm, "end": v(488.95, 111.13) * mm});
            skLineSegment(sketch, "E30.left", {"start": v(412.75, 60.33) * mm, "end": v(412.75, 111.13) * mm});
            skLineSegment(sketch, "E30.right", {"start": v(488.95, 60.33) * mm, "end": v(488.95, 111.13) * mm});
            skSolve(sketch);
        }
        {
            var Q0;
            Q0 = qSketchRegion(id + "F60", true);
            extrude(context, id + "F61", {"entities" : qUnion([Q0]), "depth" : 6.35 * mm, "offsetDistance" : 25.4 * mm});
        }
        {
            var Q0;
            Q0=makeQuery(id+"F59.opExtrude","SWEPT_FACE",FACE,{"disambiguationData":[OSD([sQuery(id+"F58.wireOp",EDGE,"E29.bottom")])]});
            var sketch = newSketch(context, id + "F62", { "sketchPlane" : qUnion([Q0])});
            skLineSegment(sketch, "E31.bottom", {"start": v(412.75, 79.38) * mm, "end": v(488.95, 79.38) * mm});
            skLineSegment(sketch, "E31.top", {"start": v(412.75, 28.58) * mm, "end": v(488.95, 28.58) * mm});
            skLineSegment(sketch, "E31.left", {"start": v(412.75, 79.38) * mm, "end": v(412.75, 28.58) * mm});
            skLineSegment(sketch, "E31.right", {"start": v(488.95, 79.38) * mm, "end": v(488.95, 28.58) * mm});
            skSolve(sketch);
        }
        {
            var Q0;
            Q0 = qSketchRegion(id + "F62", true);
            extrude(context, id + "F63", {"entities" : qUnion([Q0]), "depth" : 6.35 * mm, "offsetDistance" : 25.4 * mm});
        }
        {
            var Q0;
            Q0=makeQuery(id+"F25.opExtrude","SWEPT_FACE",FACE,{"disambiguationData":[OSD([sQuery(id+"F24.wireOp",EDGE,"E11.top")])]});
            var sketch = newSketch(context, id + "F64", { "sketchPlane" : qUnion([Q0])});
            skLineSegment(sketch, "E32.bottom", {"start": v(-228.6, 98.43) * mm, "end": v(495.3, 98.43) * mm});
            skLineSegment(sketch, "E32.top", {"start": v(-228.6, 9.52) * mm, "end": v(495.3, 9.52) * mm});
            skLineSegment(sketch, "E32.left", {"start": v(-228.6, 98.43) * mm, "end": v(-228.6, 9.52) * mm});
            skLineSegment(sketch, "E32.right", {"start": v(495.3, 98.43) * mm, "end": v(495.3, 9.52) * mm});
            skSolve(sketch);
        }
        {
            var Q0;
            Q0 = qSketchRegion(id + "F64", true);
            extrude(context, id + "F65", {"entities" : qUnion([Q0]), "depth" : 6.35 * mm, "offsetDistance" : 25.4 * mm});
        }
    });
